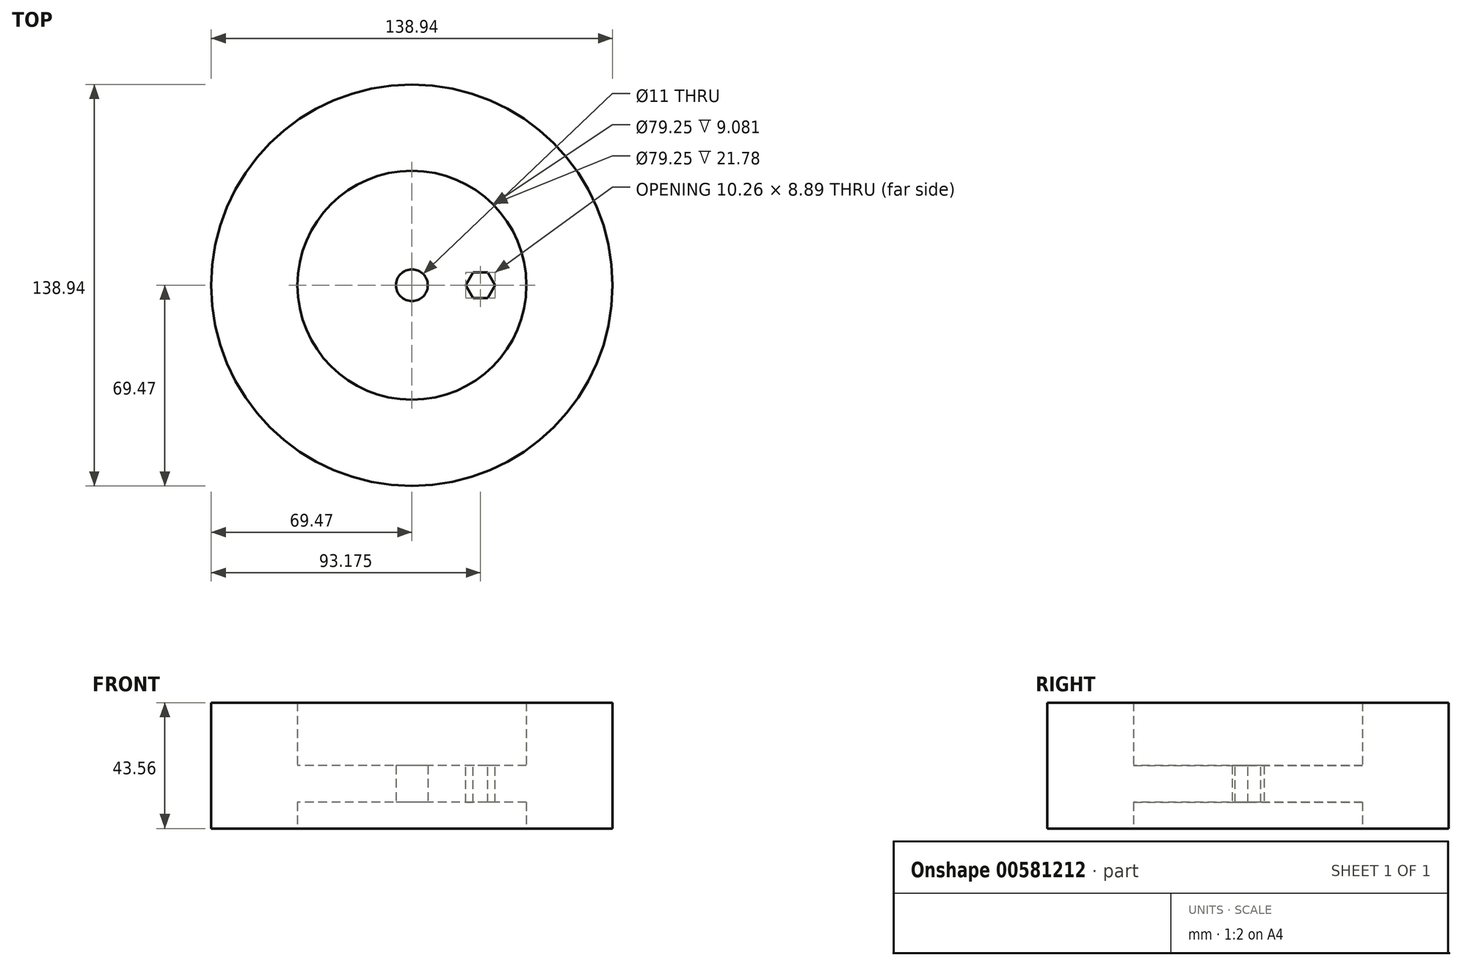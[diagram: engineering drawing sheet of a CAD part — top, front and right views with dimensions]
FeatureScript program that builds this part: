
annotation { "Feature Type Name" : "Feature", "Feature Type Description" : "" }
export const myFeature = defineFeature(function(context is Context, id is Id, definition is map)
    precondition{}
    {
        {
            var Q0;
            Q0=qCreatedBy(makeId("Top.planeOp"),FACE);
            var sketch = newSketch(context, id + "F0", { "sketchPlane" : qUnion([Q0])});
            skCircle(sketch, "E0", {"center": v(0, 0) * mm, "radius": 5.5 * mm});
            skCircle(sketch, "E1", {"center": v(0, 0) * mm, "radius": 39.62 * mm});
            skSolve(sketch);
        }
        {
            var Q0;
            Q0=makeQuery(id+"F0.imprint","IMPRINT",FACE,{"disambiguationData":[TD([[makeQuery(id+"F0.imprint","IMPRINT",EDGE,{"derivedFrom":sQuery(id+"F0.wireOp",EDGE,"E0")}),-1.0]])]});
            extrude(context, id + "F1", {"entities" : qUnion([Q0]), "depth" : 12.7 * mm, "offsetDistance" : 25.4 * mm});
        }
        {
            var Q0;
            Q0=makeQuery(id+"F1.opExtrude","CAP_FACE",FACE,{"disambiguationData":[OSD([sQuery(id+"F0.wireOp",EDGE,"E0"),sQuery(id+"F0.wireOp",EDGE,"E1")])],"isStart":false});
            var sketch = newSketch(context, id + "F2", { "sketchPlane" : qUnion([Q0])});
            skCircle(sketch, "E2", {"center": v(0, 0) * mm, "radius": 69.47 * mm});
            skSolve(sketch);
        }
        {
            var Q0;
            Q0=makeQuery(id+"F2.imprint","IMPRINT",FACE,{"disambiguationData":[TD([[makeQuery(id+"F2.imprint","IMPRINT",EDGE,{"derivedFrom":sQuery(id+"F2.wireOp",EDGE,"E2")}),1.0]])]});
            extrude(context, id + "F3", {"entities" : qUnion([Q0]), "operationType" : NewBodyOperationType.ADD, "endBound" : BoundingType.SYMMETRIC, "depth" : 43.56 * mm, "offsetDistance" : 25.4 * mm});
        }
        {
            var Q0;
            Q0=makeQuery(id+"F1.opExtrude","CAP_FACE",FACE,{"disambiguationData":[OSD([sQuery(id+"F0.wireOp",EDGE,"E0"),sQuery(id+"F0.wireOp",EDGE,"E1")])],"isStart":false});
            var sketch = newSketch(context, id + "F4", { "sketchPlane" : qUnion([Q0])});
            skCircle(sketch, "E3.cCircle", {"center": v(23.7, 0) * mm, "radius": 4.44 * mm, "construction": true});
            skLineSegment(sketch, "E3.0", {"start": v(26.27, -4.44) * mm, "end": v(21.14, -4.44) * mm});
            skLineSegment(sketch, "E3.1", {"start": v(21.14, -4.44) * mm, "end": v(18.57, 0) * mm});
            skLineSegment(sketch, "E3.2", {"start": v(18.57, 0) * mm, "end": v(21.14, 4.44) * mm});
            skLineSegment(sketch, "E3.3", {"start": v(21.14, 4.44) * mm, "end": v(26.27, 4.44) * mm});
            skLineSegment(sketch, "E3.4", {"start": v(26.27, 4.44) * mm, "end": v(28.84, 0) * mm});
            skLineSegment(sketch, "E3.5", {"start": v(28.84, 0) * mm, "end": v(26.27, -4.44) * mm});
            skPoint(sketch, "E3.0.midPoint", {"position": v(23.7, -4.44) * mm});
            skSolve(sketch);
        }
        {
            var Q0;
            Q0 = qSketchRegion(id + "F4", true);
            extrude(context, id + "F5", {"entities" : qUnion([Q0]), "operationType" : NewBodyOperationType.REMOVE, "oppositeDirection" : true, "depth" : 45.2 * mm, "offsetDistance" : 25.4 * mm});
        }
    });
